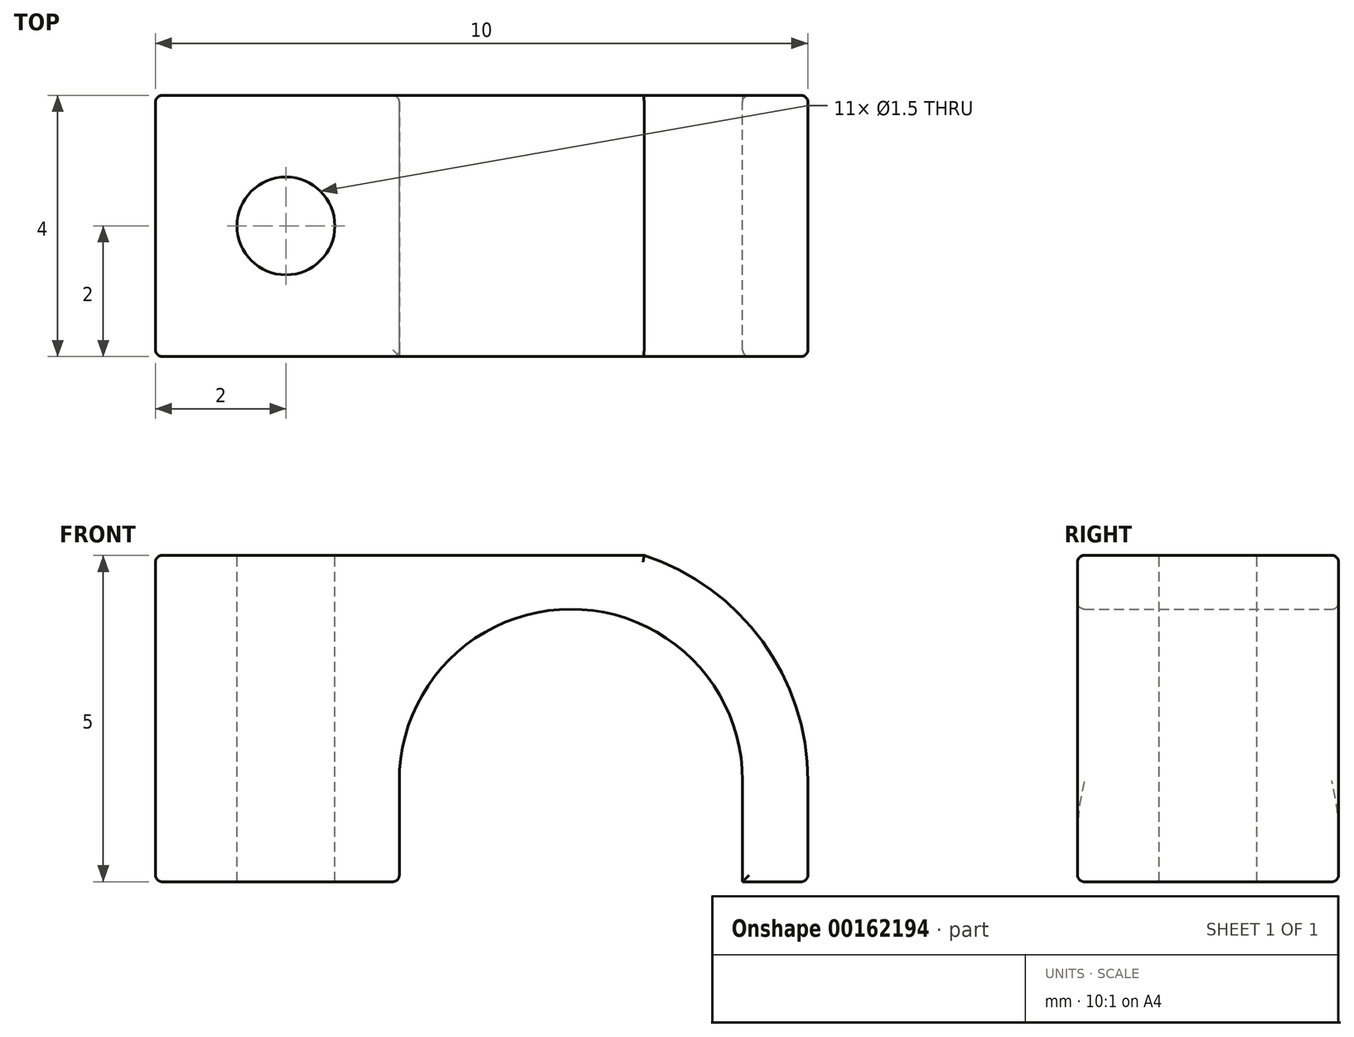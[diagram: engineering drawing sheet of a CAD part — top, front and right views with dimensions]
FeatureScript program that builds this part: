
annotation { "Feature Type Name" : "Feature", "Feature Type Description" : "" }
export const myFeature = defineFeature(function(context is Context, id is Id, definition is map)
    precondition{}
    {
        {
            var Q0;
            Q0=qCreatedBy(makeId("Front.planeOp"),FACE);
            var sketch = newSketch(context, id + "F0", { "sketchPlane" : qUnion([Q0])});
            skLineSegment(sketch, "E0.bottom", {"start": v(0, 0) * mm, "end": v(3.74, 0) * mm});
            skLineSegment(sketch, "E0.top", {"start": v(0, 5) * mm, "end": v(7.5, 5) * mm});
            skLineSegment(sketch, "E0.left", {"start": v(0, 0) * mm, "end": v(0, 5) * mm});
            skLineSegment(sketch, "E0.right", {"start": v(10, 0) * mm, "end": v(10, 1.55) * mm});
            skLineSegment(sketch, "E1", {"start": v(9, 0) * mm, "end": v(9, 1.56) * mm});
            skLineSegment(sketch, "E2", {"start": v(3.74, 0) * mm, "end": v(3.74, 1.54) * mm});
            skLineSegment(sketch, "E3", {"start": v(3.74, 1.54) * mm, "end": v(3.74, 1.54) * mm});
            skArc(sketch, "E4", {"start": v(9, 1.55) * mm, "mid": v(6.36, 4.18) * mm, "end": v(3.74, 1.54) * mm});
            skLineSegment(sketch, "E5.trimOffspring", {"start": v(9, 1.56) * mm, "end": v(9, 1.56) * mm});
            skLineSegment(sketch, "E6.trimOffspring", {"start": v(9, 0) * mm, "end": v(10, 0) * mm});
            skArc(sketch, "E7", {"start": v(5.25, 5) * mm, "mid": v(3.43, 3.68) * mm, "end": v(2.74, 1.55) * mm});
            skArc(sketch, "E8.trimOffspring", {"start": v(9.65, 0) * mm, "mid": v(9.7, 2.99) * mm, "end": v(7.5, 5) * mm});
            skSolve(sketch);
        }
        {
            var Q0;
            Q0 = qSketchRegion(id + "F0", true);
            extrude(context, id + "F1", {"entities" : qUnion([Q0]), "depth" : 4 * mm});
        }
        {
            var Q0;
            Q0=makeQuery(id+"F1.opExtrude","SWEPT_FACE",FACE,{"disambiguationData":[OSD([sQuery(id+"F0.wireOp",EDGE,"E0.top")])]});
            var sketch = newSketch(context, id + "F2", { "sketchPlane" : qUnion([Q0])});
            skCircle(sketch, "E9", {"center": v(2, -2) * mm, "radius": 2 * mm});
            skCircle(sketch, "E10", {"center": v(2, -2) * mm, "radius": 0.75 * mm});
            skSolve(sketch);
        }
        {
            var Q0;
            Q0=makeQuery(id+"F1.opExtrude","CAP_EDGE",EDGE,{"disambiguationData":[OSD([sQuery(id+"F0.wireOp",EDGE,"E0.top")])],"isStart":false});
            var Q1;
            Q1=makeQuery(id+"F1.opExtrude","SWEPT_EDGE",EDGE,{"disambiguationData":[OSD([sQuery(id+"F0.wireOp",EDGE,"E0.top"),sQuery(id+"F0.wireOp",EDGE,"E0.left")])]});
            var Q2;
            Q2=makeQuery(id+"F1.opExtrude","CAP_EDGE",EDGE,{"disambiguationData":[OSD([sQuery(id+"F0.wireOp",EDGE,"E0.left")])],"isStart":false});
            var Q3;
            Q3=makeQuery(id+"F1.opExtrude","CAP_EDGE",EDGE,{"disambiguationData":[OSD([sQuery(id+"F0.wireOp",EDGE,"E4")])],"isStart":false});
            var Q4;
            Q4=makeQuery(id+"F1.opExtrude","SWEPT_EDGE",EDGE,{"disambiguationData":[OSD([sQuery(id+"F0.wireOp",EDGE,"E0.bottom"),sQuery(id+"F0.wireOp",EDGE,"E2")])]});
            var Q5;
            Q5=makeQuery(id+"F1.opExtrude","CAP_EDGE",EDGE,{"disambiguationData":[OSD([sQuery(id+"F0.wireOp",EDGE,"E0.bottom")])],"isStart":false});
            var Q6;
            Q6=makeQuery(id+"F1.opExtrude","CAP_EDGE",EDGE,{"disambiguationData":[OSD([sQuery(id+"F0.wireOp",EDGE,"E6.trimOffspring")])],"isStart":false});
            var Q7;
            Q7=makeQuery(id+"F1.opExtrude","SWEPT_EDGE",EDGE,{"disambiguationData":[OSD([sQuery(id+"F0.wireOp",EDGE,"E0.right"),sQuery(id+"F0.wireOp",EDGE,"E6.trimOffspring")])]});
            var Q8;
            Q8=makeQuery(id+"F1.opExtrude","CAP_EDGE",EDGE,{"disambiguationData":[OSD([sQuery(id+"F0.wireOp",EDGE,"E6.trimOffspring")])],"isStart":true});
            var Q9;
            Q9=makeQuery(id+"F1.opExtrude","CAP_EDGE",EDGE,{"disambiguationData":[OSD([sQuery(id+"F0.wireOp",EDGE,"E0.right")])],"isStart":true});
            var Q10;
            Q10=makeQuery(id+"F1.opExtrude","CAP_EDGE",EDGE,{"disambiguationData":[OSD([sQuery(id+"F0.wireOp",EDGE,"E0.right")])],"isStart":false});
            var Q11;
            Q11=makeQuery(id+"F1.opExtrude","CAP_EDGE",EDGE,{"disambiguationData":[OSD([sQuery(id+"F0.wireOp",EDGE,"E2")])],"isStart":true});
            var Q12;
            Q12=makeQuery(id+"F1.opExtrude","CAP_EDGE",EDGE,{"disambiguationData":[OSD([sQuery(id+"F0.wireOp",EDGE,"E0.top")])],"isStart":true});
            var Q13;
            Q13=makeQuery(id+"F1.opExtrude","CAP_EDGE",EDGE,{"disambiguationData":[OSD([sQuery(id+"F0.wireOp",EDGE,"E0.left")])],"isStart":true});
            var Q14;
            Q14=makeQuery(id+"F1.opExtrude","CAP_EDGE",EDGE,{"disambiguationData":[OSD([sQuery(id+"F0.wireOp",EDGE,"E0.bottom")])],"isStart":true});
            var Q15;
            Q15=makeQuery(id+"F1.opExtrude","SWEPT_EDGE",EDGE,{"disambiguationData":[OSD([sQuery(id+"F0.wireOp",EDGE,"E0.bottom"),sQuery(id+"F0.wireOp",EDGE,"E0.left")])]});
            fillet(context, id + "F3", {"entities" : qUnion([Q0, Q1, Q2, Q3, Q4, Q5, Q6, Q7, Q8, Q9, Q10, Q11, Q12, Q13, Q14, Q15]), "radius" : 0.1 * mm, "tangentPropagation" : true, "allowEdgeOverflow" : false});
        }
        {
            var Q0;
            Q0=makeQuery(id+"F2.imprint","IMPRINT",FACE,{"disambiguationData":[TD([[makeQuery(id+"F2.imprint","IMPRINT",EDGE,{"derivedFrom":sQuery(id+"F2.wireOp",EDGE,"E10")}),1.0]])]});
            extrude(context, id + "F4", {"entities" : qUnion([Q0]), "operationType" : NewBodyOperationType.REMOVE, "oppositeDirection" : true, "depth" : 25 * mm});
        }
    });
